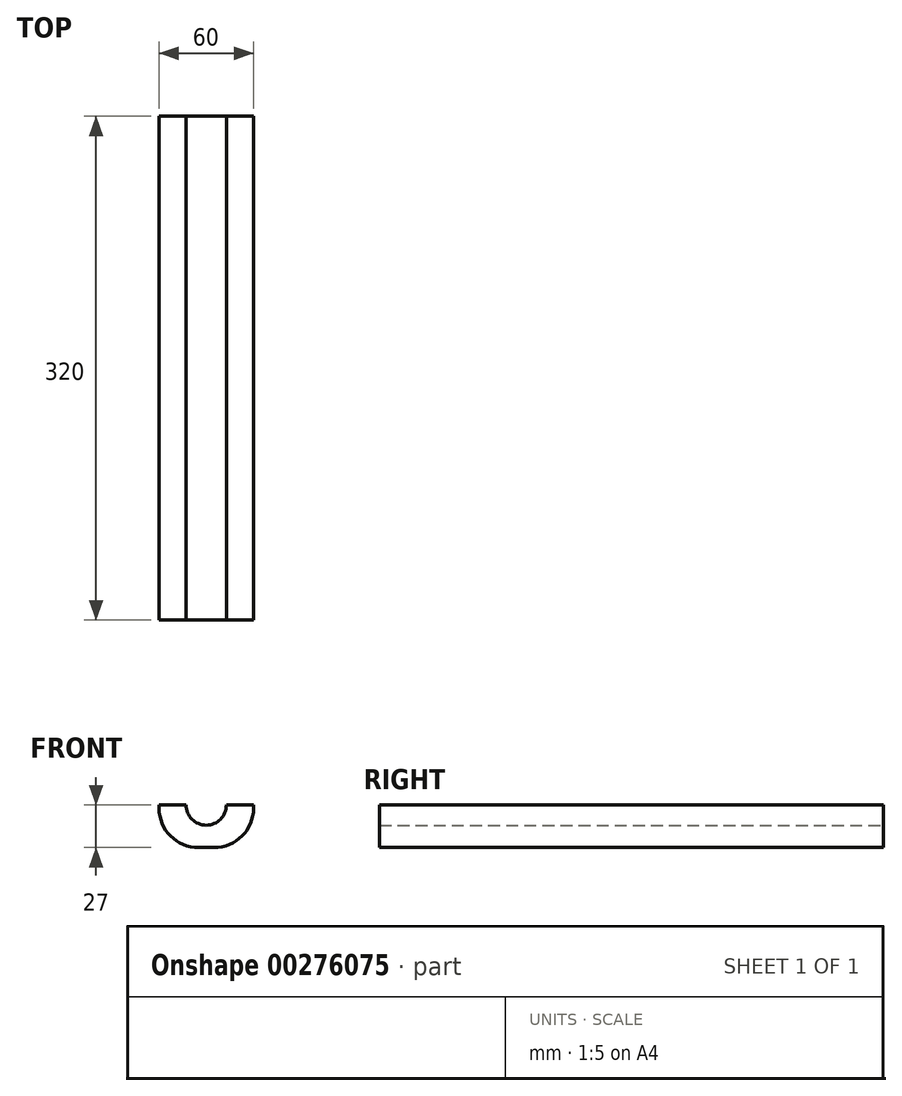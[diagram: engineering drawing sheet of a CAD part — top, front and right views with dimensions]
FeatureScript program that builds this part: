
annotation { "Feature Type Name" : "Feature", "Feature Type Description" : "" }
export const myFeature = defineFeature(function(context is Context, id is Id, definition is map)
    precondition{}
    {
        {
            var Q0;
            Q0=qCreatedBy(makeId("Front.planeOp"),FACE);
            var sketch = newSketch(context, id + "F0", { "sketchPlane" : qUnion([Q0])});
            skLineSegment(sketch, "E0.bottom", {"start": v(30, -13.5) * mm, "end": v(-30, -13.5) * mm});
            skLineSegment(sketch, "E0.top", {"start": v(30, 13.5) * mm, "end": v(-30, 13.5) * mm});
            skLineSegment(sketch, "E0.left", {"start": v(30, -13.5) * mm, "end": v(30, 13.5) * mm});
            skLineSegment(sketch, "E0.right", {"start": v(-30, -13.5) * mm, "end": v(-30, 13.5) * mm});
            skPoint(sketch, "E0.middle", {"position": v(0, 0) * mm});
            skCircle(sketch, "E1", {"center": v(0, 13.5) * mm, "radius": 12.75 * mm});
            skSolve(sketch);
        }
        {
            var Q0;
            Q0=makeQuery(id+"F0.imprint","IMPRINT",FACE,{"disambiguationData":[TD([[makeQuery(id+"F0.imprint","IMPRINT",EDGE,{"derivedFrom":sQuery(id+"F0.wireOp",EDGE,"E0.bottom")}),-1.0]])]});
            extrude(context, id + "F1", {"entities" : qUnion([Q0]), "endBound" : BoundingType.SYMMETRIC, "depth" : 320 * mm});
        }
        {
            var Q0;
            Q0=makeQuery(id+"F1.opExtrude","SWEPT_EDGE",EDGE,{"disambiguationData":[OSD([sQuery(id+"F0.wireOp",EDGE,"E0.bottom"),sQuery(id+"F0.wireOp",EDGE,"E0.left")])]});
            var Q1;
            Q1=makeQuery(id+"F1.opExtrude","SWEPT_EDGE",EDGE,{"disambiguationData":[OSD([sQuery(id+"F0.wireOp",EDGE,"E0.bottom"),sQuery(id+"F0.wireOp",EDGE,"E0.right")])]});
            fillet(context, id + "F2", {"entities" : qUnion([Q0, Q1]), "radius" : 25 * mm, "tangentPropagation" : true, "allowEdgeOverflow" : false});
        }
    });
